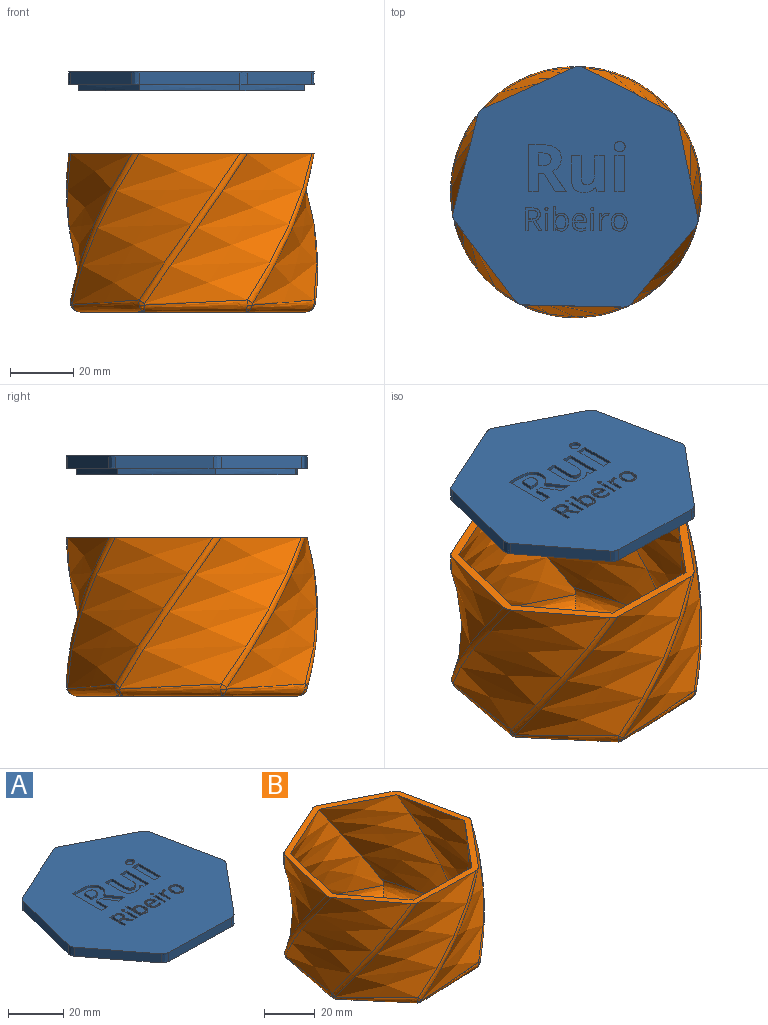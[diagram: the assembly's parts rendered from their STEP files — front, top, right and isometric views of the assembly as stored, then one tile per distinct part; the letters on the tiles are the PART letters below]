
ASSEMBLY  parts=2 mates=1
PART A: 201 faces, bbox 77.6x76.2x6.1 mm
  f0: plane 77.5x76.05mm, normal (0,0,1), area 4027.8mm2, adj f1,f2,f3,f4,f5,f6,f7,f8
  f1: extruded ~4x2.32mm, area 10.8mm2, adj f0,f2,f14,f15
  f2: plane 31.81x4mm, normal (-0.02,-1,0), area 127.3mm2, adj f0,f1,f3,f15
  f3: extruded ~4x2.37mm, area 10.8mm2, adj f0,f2,f4,f15
  f4: plane 24.44x20.38mm, normal (0.77,-0.64,0), area 127.3mm2, adj f0,f3,f5,f15
  f5: extruded ~4x2.53mm, area 10.8mm2, adj f0,f4,f6,f15
  f6: plane 31.17x6.4mm, normal (0.98,0.2,0), area 127.3mm2, adj f0,f5,f7,f15
  f7: extruded ~4x2.07mm, area 10.8mm2, adj f0,f6,f8,f15
  f8: plane 28.36x14.43mm, normal (0.45,0.89,0), area 127.3mm2, adj f0,f7,f9,f15
  f9: extruded ~4x2.6mm, area 10.8mm2, adj f0,f8,f10,f15
  f10: plane 28.97x13.18mm, normal (-0.41,0.91,0), area 127.3mm2, adj f0,f9,f11,f15
  f11: extruded ~4x2mm, area 10.8mm2, adj f0,f10,f12,f15
  f12: plane 30.86x7.76mm, normal (-0.97,0.24,0), area 127.3mm2, adj f0,f11,f13,f15
  f13: extruded ~4x2.55mm, area 10.8mm2, adj f0,f12,f14,f15
  f14: plane 25.31x19.29mm, normal (-0.8,-0.61,0), area 127.3mm2, adj f0,f1,f13,f15
  f15: plane 77.64x76.2mm, normal (0,0,-1), area 703.3mm2, adj f1,f2,f3,f4,f5,f6,f7,f8
  f16: extruded ~31.72x2mm, area 63.5mm2, adj f15,f17,f21,f23
  f17: extruded ~24.37x20.32mm, area 63.5mm2, adj f15,f16,f18,f23
  f18: extruded ~31.08x6.38mm, area 63.5mm2, adj f15,f17,f19,f23
  f19: extruded ~28.28x14.39mm, area 63.5mm2, adj f15,f18,f20,f23
  f20: extruded ~28.88x13.14mm, area 63.5mm2, adj f15,f19,f22,f23
  f21: extruded ~25.23x19.24mm, area 63.5mm2, adj f15,f16,f22,f23
  f22: extruded ~30.77x7.73mm, area 63.5mm2, adj f15,f20,f21,f23
  f23: plane 71.42x69.98mm, normal (0,0,-1), area 3672.8mm2, adj f16,f17,f18,f19,f20,f21,f22
  f24: plane 1.46x1mm, normal (0.96,0.28,0), area 1.5mm2, adj f0,f25,f40,f41
  f25: plane 2.38x1mm, normal (0,1,0), area 2.4mm2, adj f0,f24,f26,f41
  f26: plane 11.37x1mm, normal (-1,0,0), area 11.4mm2, adj f0,f25,f27,f41
  f27: plane 3.1x1mm, normal (0,-1,0), area 3.1mm2, adj f0,f26,f28,f41
  f28: plane 5.35x1mm, normal (1,0,0), area 5.4mm2, adj f0,f27,f29,f41
  f29: extruded ~2.88x1mm, area 3mm2, adj f0,f28,f30,f41
  f30: extruded ~1.88x1mm, area 2.2mm2, adj f0,f29,f31,f41
  f31: extruded ~1.4x1mm, area 1.6mm2, adj f0,f30,f32,f41
  f32: extruded ~1.85x1mm, area 1.9mm2, adj f0,f31,f33,f41
  f33: plane 6.64x1mm, normal (-1,0,0), area 6.6mm2, adj f0,f32,f34,f41
  f34: plane 3.1x1mm, normal (0,-1,0), area 3.1mm2, adj f0,f33,f35,f41
  f35: plane 7.42x1mm, normal (1,0,0), area 7.4mm2, adj f0,f34,f36,f41
  f36: extruded ~3.09x1.02mm, area 3.3mm2, adj f0,f35,f37,f41
  f37: extruded ~3.02x1.07mm, area 3.3mm2, adj f0,f36,f38,f41
  f38: extruded ~2.09x1mm, area 2.1mm2, adj f0,f37,f39,f41
  f39: extruded ~1.41x1.23mm, area 1.9mm2, adj f0,f38,f40,f41
  f40: plane 1x0.16mm, normal (0,1,0), area 0.2mm2, adj f0,f24,f39,f41
  f41: plane 11.58x10.5mm, normal (0,0,1), area 79mm2, adj f24,f25,f26,f27,f28,f29,f30,f31
  f42: extruded ~1.59x1mm, area 1.7mm2, adj f43,f58,f59,f197
  f43: extruded ~1.58x1mm, area 1.7mm2, adj f42,f44,f59,f197
  f44: extruded ~1.22x1mm, area 1.4mm2, adj f43,f45,f59,f197
  f45: extruded ~1.24x1mm, area 1.4mm2, adj f44,f46,f59,f197
  f46: extruded ~1.57x1mm, area 1.7mm2, adj f45,f47,f59,f197
  f47: extruded ~1.59x1mm, area 1.7mm2, adj f46,f48,f59,f197
  f48: extruded ~1.23x1mm, area 1.4mm2, adj f47,f58,f59,f197
  f49: extruded ~2.07x1mm, area 2.2mm2, adj f0,f50,f57,f59
  f50: extruded ~2.05x1mm, area 2.2mm2, adj f0,f49,f51,f59
  f51: extruded ~1.81x1mm, area 2mm2, adj f0,f50,f52,f59
  f52: extruded ~1.84x1mm, area 2.1mm2, adj f0,f51,f53,f59
  f53: extruded ~2.07x1mm, area 2.2mm2, adj f0,f52,f54,f59
  f54: extruded ~1.5x1mm, area 1.5mm2, adj f0,f53,f55,f59
  f55: extruded ~1x0.98mm, area 1.3mm2, adj f0,f54,f56,f59
  f56: extruded ~1.29x1mm, area 1.4mm2, adj f0,f55,f57,f59
  f57: extruded ~1.85x1mm, area 2.1mm2, adj f0,f49,f56,f59
  f58: extruded ~1.22x1mm, area 1.4mm2, adj f42,f48,f59,f197
  f59: plane 5.63x4.99mm, normal (0,0,1), area 11.3mm2, adj f42,f43,f44,f45,f46,f47,f48,f49
  f60: extruded ~1.04x1mm, area 1.2mm2, adj f61,f78,f79,f198
  f61: extruded ~1x0.99mm, area 1.1mm2, adj f60,f62,f79,f198
  f62: extruded ~1.19x1mm, area 1.3mm2, adj f61,f63,f79,f198
  f63: plane 2.84x1mm, normal (0,-1,0), area 2.8mm2, adj f62,f78,f79,f198
  f64: extruded ~1.9x1mm, area 2.1mm2, adj f0,f65,f77,f79
  f65: extruded ~1x0.94mm, area 0.9mm2, adj f0,f64,f66,f79
  f66: extruded ~1x0.82mm, area 0.9mm2, adj f0,f65,f67,f79
  f67: plane 1x0.73mm, normal (-1,0,0), area 0.7mm2, adj f0,f66,f68,f79
  f68: extruded ~1.73x1mm, area 1.8mm2, adj f0,f67,f69,f79
  f69: extruded ~1.29x1mm, area 1.4mm2, adj f0,f68,f70,f79
  f70: extruded ~1.45x1mm, area 1.6mm2, adj f0,f69,f71,f79
  f71: plane 3.74x1mm, normal (0,1,0), area 3.7mm2, adj f0,f70,f72,f79
  f72: plane 1x0.52mm, normal (-1,0,0), area 0.5mm2, adj f0,f71,f73,f79
  f73: extruded ~1.77x1mm, area 1.9mm2, adj f0,f72,f74,f79
  f74: extruded ~1.61x1mm, area 1.8mm2, adj f0,f73,f75,f79
  f75: extruded ~1.74x1mm, area 2mm2, adj f0,f74,f76,f79
  f76: extruded ~2.09x1mm, area 2.2mm2, adj f0,f75,f77,f79
  f77: extruded ~2.04x1mm, area 2.2mm2, adj f0,f64,f76,f79
  f78: extruded ~1.18x1mm, area 1.3mm2, adj f60,f63,f79,f198
  f79: plane 5.63x4.59mm, normal (0,0,1), area 11.8mm2, adj f60,f61,f62,f63,f64,f65,f66,f67
  f80: extruded ~1.21x1mm, area 1.4mm2, adj f81,f102,f103,f199
  f81: extruded ~1.15x1mm, area 1.3mm2, adj f80,f82,f103,f199
  f82: extruded ~1.58x1mm, area 1.6mm2, adj f81,f83,f103,f199
  f83: extruded ~1.59x1mm, area 1.7mm2, adj f82,f84,f103,f199
  f84: extruded ~1.13x1mm, area 1.3mm2, adj f83,f85,f103,f199
  f85: extruded ~1.22x1mm, area 1.4mm2, adj f84,f86,f103,f199
  f86: extruded ~1.64x1mm, area 1.7mm2, adj f85,f102,f103,f199
  f87: extruded ~1.66x1mm, area 1.9mm2, adj f0,f88,f101,f103
  f88: extruded ~1.7x1mm, area 2mm2, adj f0,f87,f89,f103
  f89: plane 1x0.04mm, normal (0,-1,0), area 0mm2, adj f0,f88,f90,f103
  f90: extruded ~1.13x1mm, area 1.1mm2, adj f0,f89,f91,f103
  f91: plane 1.87x1mm, normal (-1,0,0), area 1.9mm2, adj f0,f90,f92,f103
  f92: plane 1x0.82mm, normal (0,-1,0), area 0.8mm2, adj f0,f91,f93,f103
  f93: plane 7.71x1mm, normal (1,0,0), area 7.7mm2, adj f0,f92,f94,f103
  f94: plane 1x0.59mm, normal (0,1,0), area 0.6mm2, adj f0,f93,f95,f103
  f95: plane 1x0.7mm, normal (-0.97,0.24,0), area 0.7mm2, adj f0,f94,f96,f103
  f96: plane 1x0.06mm, normal (0,1,0), area 0.1mm2, adj f0,f95,f97,f103
  f97: extruded ~1x0.73mm, area 1mm2, adj f0,f96,f98,f103
  f98: extruded ~1x0.97mm, area 1mm2, adj f0,f97,f99,f103
  f99: extruded ~1.66x1mm, area 1.9mm2, adj f0,f98,f100,f103
  f100: extruded ~2.08x1mm, area 2.2mm2, adj f0,f99,f101,f103
  f101: extruded ~2.07x1mm, area 2.2mm2, adj f0,f87,f100,f103
  f102: extruded ~1.63x1mm, area 1.7mm2, adj f80,f86,f103,f199
  f103: plane 7.81x4.78mm, normal (0,0,1), area 14.3mm2, adj f80,f81,f82,f83,f84,f85,f86,f87
  f104: plane 1.16x1mm, normal (0,-1,0), area 1.2mm2, adj f105,f121,f122,f200
  f105: plane 2.77x1mm, normal (-1,0,0), area 2.8mm2, adj f104,f106,f122,f200
  f106: plane 1.1x1mm, normal (0,1,0), area 1.1mm2, adj f105,f107,f122,f200
  f107: extruded ~1.36x1mm, area 1.4mm2, adj f106,f108,f122,f200
  f108: extruded ~1.04x1mm, area 1.2mm2, adj f107,f109,f122,f200
  f109: extruded ~1.06x1mm, area 1.2mm2, adj f108,f121,f122,f200
  f110: plane 3.01x1mm, normal (-1,0,0), area 3mm2, adj f0,f111,f120,f122
  f111: plane 1.51x1mm, normal (0,1,0), area 1.5mm2, adj f0,f110,f112,f122
  f112: plane 3.01x1.75mm, normal (0.86,0.5,0), area 3.5mm2, adj f0,f111,f113,f122
  f113: plane 1x1mm, normal (0,1,0), area 1mm2, adj f0,f112,f114,f122
  f114: plane 3.25x1.97mm, normal (-0.86,-0.52,0), area 3.8mm2, adj f0,f113,f115,f122
  f115: extruded ~1.94x1.46mm, area 2.6mm2, adj f0,f114,f116,f122
  f116: extruded ~1.54x1mm, area 1.7mm2, adj f0,f115,f117,f122
  f117: extruded ~1.97x1mm, area 2.1mm2, adj f0,f116,f118,f122
  f118: plane 1.99x1mm, normal (0,-1,0), area 2mm2, adj f0,f117,f119,f122
  f119: plane 7.24x1mm, normal (1,0,0), area 7.2mm2, adj f0,f118,f120,f122
  f120: plane 1x0.84mm, normal (0,1,0), area 0.8mm2, adj f0,f110,f119,f122
  f121: extruded ~1.31x1mm, area 1.4mm2, adj f104,f109,f122,f200
  f122: plane 7.24x5.1mm, normal (0,0,1), area 15.7mm2, adj f104,f105,f106,f107,f108,f109,f110,f111
  f123: extruded ~1.69x1.52mm, area 2.6mm2, adj f0,f124,f127,f128
  f124: extruded ~1.69x1.53mm, area 2.6mm2, adj f0,f123,f125,f128
  f125: extruded ~1.27x1mm, area 1.4mm2, adj f0,f124,f126,f128
  f126: extruded ~1.12x1mm, area 1.2mm2, adj f0,f125,f127,f128
  f127: extruded ~1.69x1.52mm, area 2.6mm2, adj f0,f123,f126,f128
  f128: plane 3.38x3.04mm, normal (0,0,1), area 8.6mm2, adj f123,f124,f125,f126,f127
  f129: plane 3.1x1mm, normal (0,1,0), area 3.1mm2, adj f0,f130,f132,f133
  f130: plane 11.37x1mm, normal (-1,0,0), area 11.4mm2, adj f0,f129,f131,f133
  f131: plane 3.1x1mm, normal (0,-1,0), area 3.1mm2, adj f0,f130,f132,f133
  f132: plane 11.37x1mm, normal (1,0,0), area 11.4mm2, adj f0,f129,f131,f133
  f133: plane 11.37x3.1mm, normal (0,0,1), area 35.3mm2, adj f129,f130,f131,f132
  f134: plane 1x0.82mm, normal (0,1,0), area 0.8mm2, adj f0,f135,f137,f138
  f135: plane 5.43x1mm, normal (-1,0,0), area 5.4mm2, adj f0,f134,f136,f138
  f136: plane 1x0.82mm, normal (0,-1,0), area 0.8mm2, adj f0,f135,f137,f138
  f137: plane 5.43x1mm, normal (1,0,0), area 5.4mm2, adj f0,f134,f136,f138
  f138: plane 5.43x0.82mm, normal (0,0,1), area 4.5mm2, adj f134,f135,f136,f137
  f139: extruded ~1x0.41mm, area 0.4mm2, adj f0,f140,f146,f147
  f140: extruded ~1x0.41mm, area 0.4mm2, adj f0,f139,f141,f147
  f141: extruded ~1x0.35mm, area 0.4mm2, adj f0,f140,f142,f147
  f142: extruded ~1x0.34mm, area 0.4mm2, adj f0,f141,f143,f147
  f143: extruded ~1x0.41mm, area 0.5mm2, adj f0,f142,f144,f147
  f144: extruded ~1x0.41mm, area 0.4mm2, adj f0,f143,f145,f147
  f145: extruded ~1x0.34mm, area 0.4mm2, adj f0,f144,f146,f147
  f146: extruded ~1x0.35mm, area 0.4mm2, adj f0,f139,f145,f147
  f147: plane 1.1x0.97mm, normal (0,0,1), area 0.9mm2, adj f139,f140,f141,f142,f143,f144,f145,f146
  f148: plane 5.71x1mm, normal (-1,0,0), area 5.7mm2, adj f0,f149,f166,f167
  f149: plane 1.68x1mm, normal (0,1,0), area 1.7mm2, adj f0,f148,f150,f167
  f150: plane 5.71x3.55mm, normal (0.85,0.53,0), area 6.7mm2, adj f0,f149,f151,f167
  f151: plane 3.5x1mm, normal (0,1,0), area 3.5mm2, adj f0,f150,f152,f167
  f152: extruded ~6.48x4.38mm, area 7.8mm2, adj f0,f151,f153,f167
  f153: extruded ~2.05x1.6mm, area 2.6mm2, adj f0,f152,f154,f167
  f154: extruded ~2.33x1mm, area 2.5mm2, adj f0,f153,f155,f167
  f155: extruded ~3.35x1.45mm, area 3.8mm2, adj f0,f154,f156,f167
  f156: extruded ~4.49x1.1mm, area 4.7mm2, adj f0,f155,f157,f167
  f157: plane 4.33x1mm, normal (0,-1,0), area 4.3mm2, adj f0,f156,f158,f167
  f158: plane 14.87x1mm, normal (1,0,0), area 14.9mm2, adj f0,f157,f166,f167
  f159: plane 1.02x1mm, normal (0,-1,0), area 1mm2, adj f160,f165,f167,f168
  f160: plane 4.02x1mm, normal (-1,0,0), area 4mm2, adj f159,f161,f167,f168
  f161: plane 1x0.96mm, normal (0,1,0), area 1mm2, adj f160,f162,f167,f168
  f162: extruded ~2.25x1mm, area 2.3mm2, adj f161,f163,f167,f168
  f163: extruded ~1.51x1mm, area 1.8mm2, adj f162,f164,f167,f168
  f164: extruded ~1.57x1mm, area 1.8mm2, adj f163,f165,f167,f168
  f165: extruded ~2.21x1mm, area 2.3mm2, adj f159,f164,f167,f168
  f166: plane 3.15x1mm, normal (0,1,0), area 3.2mm2, adj f0,f148,f158,f167
  f167: plane 14.87x11.88mm, normal (0,0,1), area 108mm2, adj f148,f149,f150,f151,f152,f153,f154,f155
  f168: plane 4.02x3.94mm, normal (0,0,1), area 14mm2, adj f159,f160,f161,f162,f163,f164,f165
  f169: extruded ~1x0.65mm, area 0.7mm2, adj f0,f170,f181,f182
  f170: extruded ~1x0.94mm, area 1mm2, adj f0,f169,f171,f182
  f171: extruded ~1x0.82mm, area 1.1mm2, adj f0,f170,f172,f182
  f172: plane 1x0.04mm, normal (0,-1,0), area 0mm2, adj f0,f171,f173,f182
  f173: plane 1.01x1mm, normal (-1,-0.09,0), area 1mm2, adj f0,f172,f174,f182
  f174: plane 1x0.68mm, normal (0,-1,0), area 0.7mm2, adj f0,f173,f175,f182
  f175: plane 5.43x1mm, normal (1,0,0), area 5.4mm2, adj f0,f174,f176,f182
  f176: plane 1x0.82mm, normal (0,1,0), area 0.8mm2, adj f0,f175,f177,f182
  f177: plane 2.91x1mm, normal (-1,0,0), area 2.9mm2, adj f0,f176,f178,f182
  f178: extruded ~1.33x1mm, area 1.4mm2, adj f0,f177,f179,f182
  f179: extruded ~1.13x1mm, area 1.3mm2, adj f0,f178,f180,f182
  f180: extruded ~1x0.59mm, area 0.6mm2, adj f0,f179,f181,f182
  f181: plane 1x0.76mm, normal (-0.99,0.15,0), area 0.8mm2, adj f0,f169,f180,f182
  f182: plane 5.53x3.13mm, normal (0,0,1), area 6.1mm2, adj f169,f170,f171,f172,f173,f174,f175,f176
  f183: extruded ~1x0.41mm, area 0.4mm2, adj f0,f184,f190,f191
  f184: extruded ~1x0.41mm, area 0.4mm2, adj f0,f183,f185,f191
  f185: extruded ~1x0.35mm, area 0.4mm2, adj f0,f184,f186,f191
  f186: extruded ~1x0.34mm, area 0.4mm2, adj f0,f185,f187,f191
  f187: extruded ~1x0.41mm, area 0.5mm2, adj f0,f186,f188,f191
  f188: extruded ~1x0.41mm, area 0.4mm2, adj f0,f187,f189,f191
  f189: extruded ~1x0.34mm, area 0.4mm2, adj f0,f188,f190,f191
  f190: extruded ~1x0.35mm, area 0.4mm2, adj f0,f183,f189,f191
  f191: plane 1.1x0.97mm, normal (0,0,1), area 0.9mm2, adj f183,f184,f185,f186,f187,f188,f189,f190
  f192: plane 1x0.82mm, normal (0,1,0), area 0.8mm2, adj f0,f193,f195,f196
  f193: plane 5.43x1mm, normal (-1,0,0), area 5.4mm2, adj f0,f192,f194,f196
  f194: plane 1x0.82mm, normal (0,-1,0), area 0.8mm2, adj f0,f193,f195,f196
  f195: plane 5.43x1mm, normal (1,0,0), area 5.4mm2, adj f0,f192,f194,f196
  f196: plane 5.43x0.82mm, normal (0,0,1), area 4.5mm2, adj f192,f193,f194,f195
  f197: plane 4.24x3.28mm, normal (0,0,1), area 11.6mm2, adj f42,f43,f44,f45,f46,f47,f48,f58
  f198: plane 2.84x1.6mm, normal (0,0,1), area 3.7mm2, adj f60,f61,f62,f63,f78
  f199: plane 4.24x3.11mm, normal (0,0,1), area 11.1mm2, adj f80,f81,f82,f83,f84,f85,f86,f102
  f200: plane 2.88x2.77mm, normal (0,0,1), area 7.2mm2, adj f104,f105,f106,f107,f108,f109,f121
PART B: 46 faces, bbox 83.8x85.5x58.4 mm
  f0: plane 71.22x69.94mm, normal (0,0,-1), area 3671mm2, adj f1,f31,f33,f34,f35,f36,f37
  f1: bspline ~33.27x28.19mm, area 151.9mm2, adj f0,f2,f3,f29,f30
  f2: bspline ~2.89x2.18mm, area 3mm2, adj f1,f30,f31
  f3: bspline ~2.94x2.18mm, area 2.9mm2, adj f1,f4,f37
  f4: bspline ~1.87x1.7mm, area 2.1mm2, adj f3,f5,f29,f37
  f5: bspline ~58.33x31.25mm, area 127.7mm2, adj f4,f6,f28,f29
  f6: plane 77.51x76.07mm, normal (0,0,1), area 591.7mm2, adj f5,f7,f10,f13,f14,f17,f18,f21
  f7: bspline ~58.33x41.02mm, area 127.7mm2, adj f6,f8,f10,f28
  f8: bspline ~1.7x1.58mm, area 2.2mm2, adj f7,f9,f28,f36
  f9: bspline ~2.75x2.36mm, area 3mm2, adj f8,f36,f37
  f10: bspline ~58.33x51.75mm, area 1515.6mm2, adj f6,f7,f11,f13,f36
  f11: bspline ~1.94x1.7mm, area 2.2mm2, adj f10,f12,f13,f35
  f12: bspline ~2.96x2.18mm, area 3.1mm2, adj f11,f35,f36
  f13: bspline ~58.33x36.5mm, area 127.7mm2, adj f6,f10,f11,f14
  f14: bspline ~63.51x58.33mm, area 1515.6mm2, adj f6,f13,f15,f17,f35
  f15: bspline ~1.7x1.5mm, area 2.2mm2, adj f14,f16,f17,f34
  f16: bspline ~2.68x2.47mm, area 2.9mm2, adj f15,f34,f35
  f17: bspline ~58.33x38.41mm, area 127.7mm2, adj f6,f14,f15,f18
  f18: bspline ~58.33x48.05mm, area 1515.6mm2, adj f6,f17,f19,f21,f34
  f19: bspline ~1.91x1.7mm, area 2.2mm2, adj f18,f20,f21,f33
  f20: bspline ~2.94x2.18mm, area 3.2mm2, adj f19,f33,f34
  f21: bspline ~58.33x40.04mm, area 127.7mm2, adj f6,f18,f19,f22
  f22: bspline ~62.66x58.33mm, area 1515.6mm2, adj f6,f21,f23,f25,f33
  f23: bspline ~1.73x1.7mm, area 2.1mm2, adj f22,f24,f25,f31
  f24: bspline ~2.42x2.13mm, area 2.3mm2, adj f23,f31,f33
  f25: bspline ~58.33x33.89mm, area 127.7mm2, adj f6,f22,f23,f26
  f26: bspline ~58.33x55.76mm, area 1515.6mm2, adj f6,f25,f27,f30,f31
  f27: bspline ~58.33x41.57mm, area 127.7mm2, adj f6,f26,f29,f30
  f28: bspline ~61.17x58.33mm, area 1515.6mm2, adj f5,f6,f7,f8,f37
  f29: bspline ~58.68x58.33mm, area 1515.6mm2, adj f1,f4,f5,f6,f27
  f30: bspline ~1.79x1.7mm, area 2.1mm2, adj f1,f2,f26,f27
  f31: bspline ~40.18x4.34mm, area 152mm2, adj f0,f2,f23,f24,f26,f32
  f32: bspline ~0.83x0.27mm, area 0mm2, adj f31,f33
  f33: bspline ~33.84x27.38mm, area 152mm2, adj f0,f19,f20,f22,f24,f32
  f34: bspline ~39.84x13mm, area 151.9mm2, adj f0,f15,f16,f18,f20
  f35: bspline ~37.79x20.12mm, area 151.9mm2, adj f0,f11,f12,f14,f16
  f36: bspline ~37.49x21.12mm, area 151.9mm2, adj f0,f8,f9,f10,f12
  f37: bspline ~39.85x11.84mm, area 151.9mm2, adj f0,f3,f4,f9,f28
  f38: plane 60.94x60.93mm, normal (0,0,1), area 2732.2mm2, adj f39,f40,f41,f42,f43,f44,f45
  f39: bspline ~45.09x9.93mm, area 236.9mm2, adj f38,f40,f45
  f40: bspline ~36.56x34.92mm, area 236.9mm2, adj f38,f39,f41
  f41: bspline ~44.67x12.07mm, area 236.9mm2, adj f38,f40,f42
  f42: bspline ~41.53x27.84mm, area 236.9mm2, adj f38,f41,f43
  f43: bspline ~43.55x21.45mm, area 236.9mm2, adj f38,f42,f44
  f44: bspline ~44.43x19.37mm, area 236.9mm2, adj f38,f43,f45
  f45: bspline ~40.24x29.75mm, area 236.9mm2, adj f38,f39,f44
PLACE A t=(5.03,-4.55,0)mm
PLACE B t=(5.03,-4.55,-21.79)mm
MATE slider B.f6 <-> A.f23  axis (0,0,1) through (5.03,-4.55,28.21)mm
